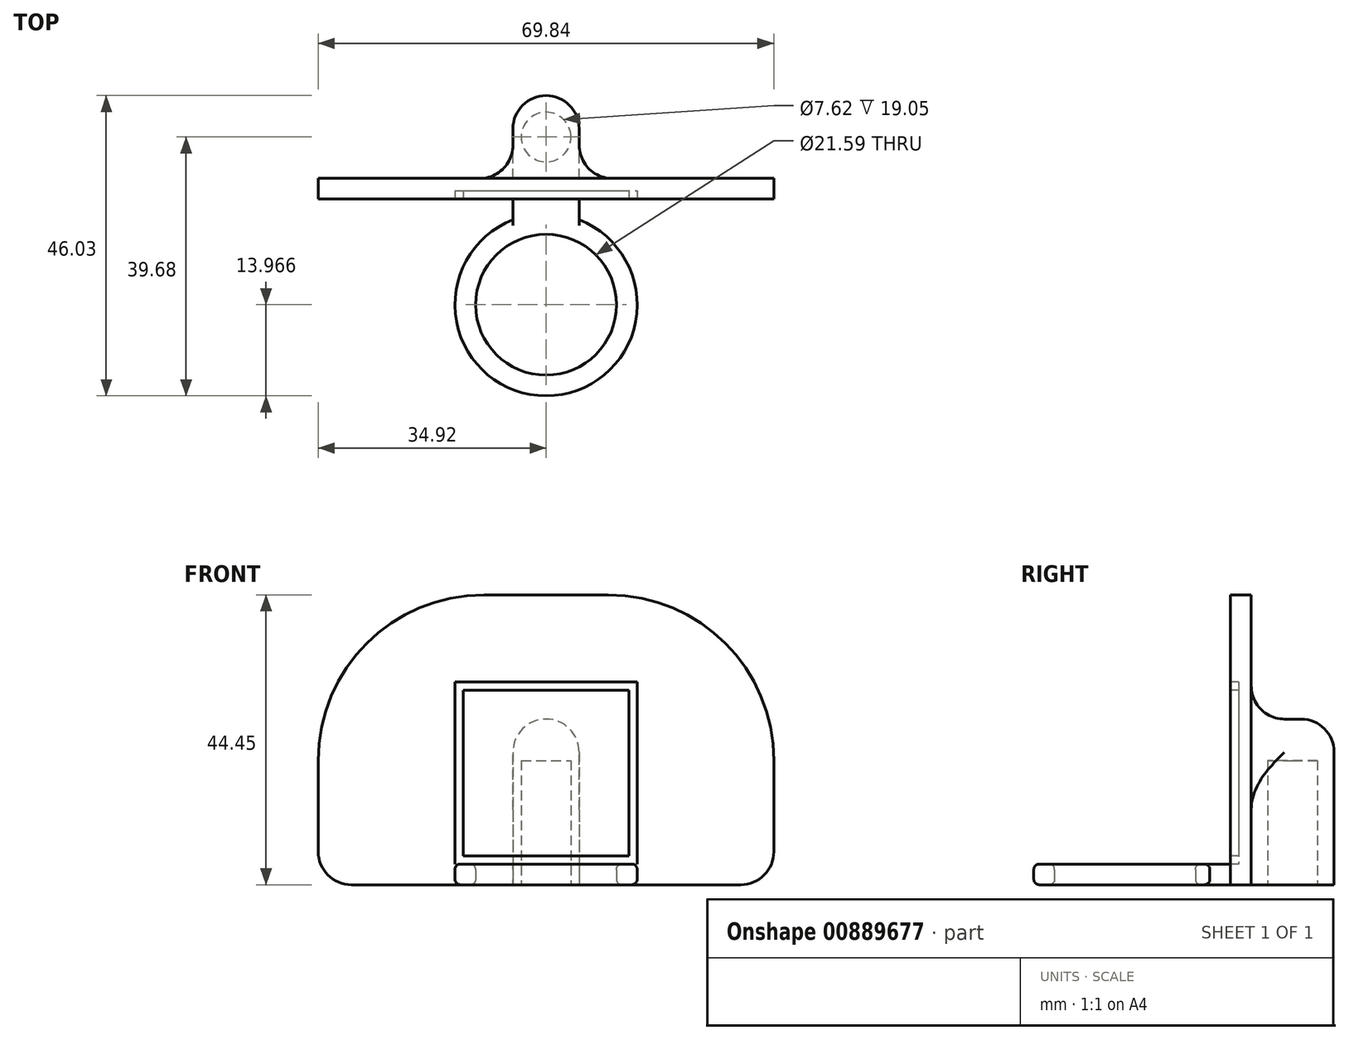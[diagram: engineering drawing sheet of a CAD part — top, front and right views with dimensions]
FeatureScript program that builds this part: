
annotation { "Feature Type Name" : "Feature", "Feature Type Description" : "" }
export const myFeature = defineFeature(function(context is Context, id is Id, definition is map)
    precondition{}
    {
        {
            var Q0;
            Q0=qCreatedBy(makeId("Front.planeOp"),FACE);
            var sketch = newSketch(context, id + "F0", { "sketchPlane" : qUnion([Q0])});
            skLineSegment(sketch, "E0.bottom", {"start": v(-34.93, 0) * mm, "end": v(34.93, 0) * mm});
            skLineSegment(sketch, "E0.top", {"start": v(-34.93, 44.45) * mm, "end": v(34.93, 44.45) * mm});
            skLineSegment(sketch, "E0.left", {"start": v(-34.93, 0) * mm, "end": v(-34.93, 44.45) * mm});
            skLineSegment(sketch, "E0.right", {"start": v(34.92, 0) * mm, "end": v(34.92, 44.45) * mm});
            skSolve(sketch);
        }
        {
            var Q0;
            Q0 = qSketchRegion(id + "F0", true);
            extrude(context, id + "F1", {"entities" : qUnion([Q0]), "depth" : 3.17 * mm, "offsetDistance" : 25.4 * mm});
        }
        {
            var Q0;
            Q0=makeQuery(id+"F1.opExtrude","SWEPT_EDGE",EDGE,{"disambiguationData":[OSD([sQuery(id+"F0.wireOp",EDGE,"E0.top"),sQuery(id+"F0.wireOp",EDGE,"E0.left")])]});
            var Q1;
            Q1=makeQuery(id+"F1.opExtrude","SWEPT_EDGE",EDGE,{"disambiguationData":[OSD([sQuery(id+"F0.wireOp",EDGE,"E0.top"),sQuery(id+"F0.wireOp",EDGE,"E0.right")])]});
            fillet(context, id + "F2", {"entities" : qUnion([Q0, Q1]), "radius" : 25.4 * mm, "tangentPropagation" : true, "allowEdgeOverflow" : false});
        }
        {
            var Q0;
            Q0=makeQuery(id+"F1.opExtrude","SWEPT_EDGE",EDGE,{"disambiguationData":[OSD([sQuery(id+"F0.wireOp",EDGE,"E0.bottom"),sQuery(id+"F0.wireOp",EDGE,"E0.left")])]});
            var Q1;
            Q1=makeQuery(id+"F1.opExtrude","SWEPT_EDGE",EDGE,{"disambiguationData":[OSD([sQuery(id+"F0.wireOp",EDGE,"E0.bottom"),sQuery(id+"F0.wireOp",EDGE,"E0.right")])]});
            fillet(context, id + "F3", {"entities" : qUnion([Q0, Q1]), "radius" : 5.08 * mm, "tangentPropagation" : true, "allowEdgeOverflow" : false});
        }
        {
            var Q0;
            Q0=makeQuery(id+"F1.opExtrude","SWEPT_FACE",FACE,{"disambiguationData":[OSD([sQuery(id+"F0.wireOp",EDGE,"E0.bottom")])]});
            var sketch = newSketch(context, id + "F4", { "sketchPlane" : qUnion([Q0])});
            skLineSegment(sketch, "E1.bottom", {"start": v(-5.08, 0) * mm, "end": v(5.08, 0) * mm});
            skLineSegment(sketch, "E1.top", {"start": v(-5.08, -12.7) * mm, "end": v(5.08, -12.7) * mm});
            skLineSegment(sketch, "E1.left", {"start": v(-5.08, 0) * mm, "end": v(-5.08, -12.7) * mm});
            skLineSegment(sketch, "E1.right", {"start": v(5.08, 0) * mm, "end": v(5.08, -12.7) * mm});
            skSolve(sketch);
        }
        {
            var Q0;
            Q0 = qSketchRegion(id + "F4", true);
            extrude(context, id + "F5", {"entities" : qUnion([Q0]), "operationType" : NewBodyOperationType.ADD, "oppositeDirection" : true, "depth" : 25.4 * mm, "offsetDistance" : 25.4 * mm});
        }
        {
            var Q0;
            Q0=makeQuery(id+"F5.boolean.opBoolean","MERGE",FACE,{"derivedFrom":[makeQuery(id+"F1.opExtrude","SWEPT_FACE",FACE,{"disambiguationData":[OSD([sQuery(id+"F0.wireOp",EDGE,"E0.bottom")])]}),makeQuery(id+"F5.opExtrude","CAP_FACE",FACE,{"disambiguationData":[OSD([sQuery(id+"F4.wireOp",EDGE,"E1.bottom"),sQuery(id+"F4.wireOp",EDGE,"E1.top"),sQuery(id+"F4.wireOp",EDGE,"E1.left"),sQuery(id+"F4.wireOp",EDGE,"E1.right")])],"isStart":true})]});
            var sketch = newSketch(context, id + "F6", { "sketchPlane" : qUnion([Q0])});
            skCircle(sketch, "E2", {"center": v(0, -6.35) * mm, "radius": 3.81 * mm});
            skSolve(sketch);
        }
        {
            var Q0;
            Q0 = qSketchRegion(id + "F6", true);
            extrude(context, id + "F7", {"entities" : qUnion([Q0]), "operationType" : NewBodyOperationType.REMOVE, "oppositeDirection" : true, "depth" : 19.05 * mm, "offsetDistance" : 25.4 * mm});
        }
        {
            var Q0;
            Q0=makeQuery(id+"F5.opExtrude","SWEPT_EDGE",EDGE,{"disambiguationData":[OSD([sQuery(id+"F4.wireOp",EDGE,"E1.top"),sQuery(id+"F4.wireOp",EDGE,"E1.left")])]});
            var Q1;
            Q1=makeQuery(id+"F5.opExtrude","SWEPT_EDGE",EDGE,{"disambiguationData":[OSD([sQuery(id+"F4.wireOp",EDGE,"E1.top"),sQuery(id+"F4.wireOp",EDGE,"E1.right")])]});
            var Q2;
            Q2=makeQuery(id+"F5.opExtrude","CAP_FACE",FACE,{"disambiguationData":[OSD([sQuery(id+"F4.wireOp",EDGE,"E1.bottom"),sQuery(id+"F4.wireOp",EDGE,"E1.top"),sQuery(id+"F4.wireOp",EDGE,"E1.left"),sQuery(id+"F4.wireOp",EDGE,"E1.right")])],"isStart":false});
            fillet(context, id + "F8", {"entities" : qUnion([Q0, Q1, Q2]), "radius" : 5.08 * mm, "tangentPropagation" : true, "allowEdgeOverflow" : false});
        }
        {
            var Q0;
            Q0=makeQuery(id+"F5.boolean.opBoolean","MERGE",FACE,{"derivedFrom":[makeQuery(id+"F1.opExtrude","SWEPT_FACE",FACE,{"disambiguationData":[OSD([sQuery(id+"F0.wireOp",EDGE,"E0.bottom")])]}),makeQuery(id+"F5.opExtrude","CAP_FACE",FACE,{"disambiguationData":[OSD([sQuery(id+"F4.wireOp",EDGE,"E1.bottom"),sQuery(id+"F4.wireOp",EDGE,"E1.top"),sQuery(id+"F4.wireOp",EDGE,"E1.left"),sQuery(id+"F4.wireOp",EDGE,"E1.right")])],"isStart":true})]});
            var sketch = newSketch(context, id + "F9", { "sketchPlane" : qUnion([Q0])});
            skLineSegment(sketch, "E3.bottom", {"start": v(-5.08, 3.17) * mm, "end": v(5.08, 3.18) * mm});
            skLineSegment(sketch, "E3.top", {"start": v(-5.08, 6.35) * mm, "end": v(-5.08, 6.35) * mm});
            skLineSegment(sketch, "E3.left", {"start": v(-5.08, 3.17) * mm, "end": v(-5.08, 6.35) * mm});
            skLineSegment(sketch, "E3.right", {"start": v(5.08, 3.18) * mm, "end": v(5.08, 6.35) * mm});
            skArc(sketch, "E4", {"start": v(5.08, 6.35) * mm, "mid": v(0, 33.33) * mm, "end": v(-5.08, 6.35) * mm});
            skCircle(sketch, "E5", {"center": v(0, 19.36) * mm, "radius": 10.8 * mm});
            skSolve(sketch);
        }
        {
            var Q0;
            Q0 = qSketchRegion(id + "F9", true);
            extrude(context, id + "F10", {"entities" : qUnion([Q0]), "operationType" : NewBodyOperationType.ADD, "oppositeDirection" : true, "depth" : 3.17 * mm, "offsetDistance" : 25.4 * mm});
        }
        {
            var Q0;
            Q0=makeQuery(id+"F10.opExtrude","CAP_EDGE",EDGE,{"disambiguationData":[OSD([sQuery(id+"F9.wireOp",EDGE,"E5")])],"isStart":false});
            var Q1;
            Q1=makeQuery(id+"F10.opExtrude","CAP_EDGE",EDGE,{"disambiguationData":[OSD([sQuery(id+"F9.wireOp",EDGE,"E4")])],"isStart":false});
            var Q2;
            Q2=makeQuery(id+"F10.opExtrude","CAP_EDGE",EDGE,{"disambiguationData":[OSD([sQuery(id+"F9.wireOp",EDGE,"E4")])],"isStart":true});
            var Q3;
            Q3=makeQuery(id+"F10.opExtrude","CAP_EDGE",EDGE,{"disambiguationData":[OSD([sQuery(id+"F9.wireOp",EDGE,"E5")])],"isStart":true});
            fillet(context, id + "F11", {"entities" : qUnion([Q0, Q1, Q2, Q3]), "radius" : 0.83 * mm, "tangentPropagation" : true, "allowEdgeOverflow" : false});
        }
        {
            var Q0;
            Q0=makeQuery(id+"F1.opExtrude","CAP_FACE",FACE,{"disambiguationData":[OSD([sQuery(id+"F0.wireOp",EDGE,"E0.bottom"),sQuery(id+"F0.wireOp",EDGE,"E0.top"),sQuery(id+"F0.wireOp",EDGE,"E0.left"),sQuery(id+"F0.wireOp",EDGE,"E0.right")])],"isStart":false});
            var sketch = newSketch(context, id + "F12", { "sketchPlane" : qUnion([Q0])});
            skLineSegment(sketch, "E6.bottom", {"start": v(-13.97, 31.12) * mm, "end": v(13.97, 31.12) * mm});
            skLineSegment(sketch, "E6.top", {"start": v(-13.97, 3.17) * mm, "end": v(13.97, 3.18) * mm});
            skLineSegment(sketch, "E6.left", {"start": v(-13.97, 31.12) * mm, "end": v(-13.97, 3.18) * mm});
            skLineSegment(sketch, "E6.right", {"start": v(13.97, 31.12) * mm, "end": v(13.97, 3.18) * mm});
            skLineSegment(sketch, "E7", {"start": v(0, 0) * mm, "end": v(0, 3.18) * mm, "construction": true});
            skLineSegment(sketch, "E8.0", {"start": v(-12.7, 29.85) * mm, "end": v(12.7, 29.85) * mm});
            skLineSegment(sketch, "E8.1", {"start": v(-12.7, 29.85) * mm, "end": v(-12.7, 4.45) * mm});
            skLineSegment(sketch, "E8.3", {"start": v(12.7, 29.85) * mm, "end": v(12.7, 4.45) * mm});
            skLineSegment(sketch, "E9", {"start": v(-12.7, 4.45) * mm, "end": v(12.7, 4.45) * mm});
            skSolve(sketch);
        }
        {
            var Q0;
            Q0 = qSketchRegion(id + "F12", true);
            extrude(context, id + "F13", {"entities" : qUnion([Q0]), "operationType" : NewBodyOperationType.REMOVE, "oppositeDirection" : true, "depth" : 1.27 * mm, "offsetDistance" : 25.4 * mm});
        }
    });
